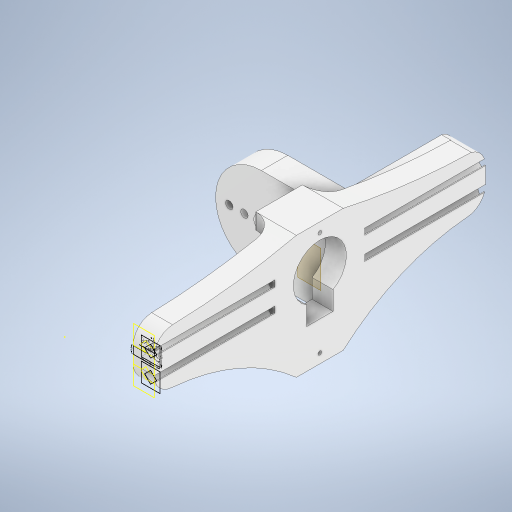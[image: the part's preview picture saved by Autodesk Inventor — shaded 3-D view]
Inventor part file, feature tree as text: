
AUTODESK INVENTOR PART (.ipt)
format: ipt  version: 2024 (Build 280153000, 153)  size: 1,017,344 bytes
history: native  units: in
note: dims shown in document units (in); Inventor stores cm internally (conversion verified against a paired STEP export)
features: other x6, projected_geometry x4, extrude x3, fillet x2, sketch x2, mirror x2, plane x1
ambient origin geometry x8: Origin, YZ Plane, XZ Plane, XY Plane, X Axis, Y Axis, Z Axis, Center Point
bodies: Solid1 (feature_tree)
feature tree (20):
  fillet  "Fillet9"  Radius=0.0886in
  other  "Axis1"
  other  "Axis2"
  other  "Plane1"
  other  "Plane2"
  other  "Plane3"
  other  "Plane4"
  sketch  "Sketch1"  dims[d5=0.0886in d6=0.0394in]
  extrude  "Extrusion1"  Depth=0.0394in
  extrude  "Extrusion2"  TaperAngle=45.0deg  [1 undecoded]
  plane  "Work Plane7"
  mirror  "Mirror1"
  extrude  "Extrusion3"  Depth=0.1969in
  mirror  "Mirror2"
  fillet  "Fillet1"  Radius=0.1969in
  projected_geometry  "Projected Loop1"
  projected_geometry  "Projected Loop2"
  projected_geometry  "Projected Loop6"
  projected_geometry  "Projected Loop7"
  sketch  "Sketch3"  dims[d7=0.0in d8=45.0deg d9=0.1969in d10=0.1969in d11=0.3937in d12=0.0in d13=0.0in d14=0.0in d18=0.0787in d19=-1.7283in d20=0.3937in d21=0.3937in d22=0.8912in d23=0.1635in d24=0.0in d25=0.0in d26=0.0039in]
note: 1 required parameter value undecoded (feature->parameter linkage not recoverable at this tier; creation-order binding heuristic only, values carry confidence <= 0.55)
